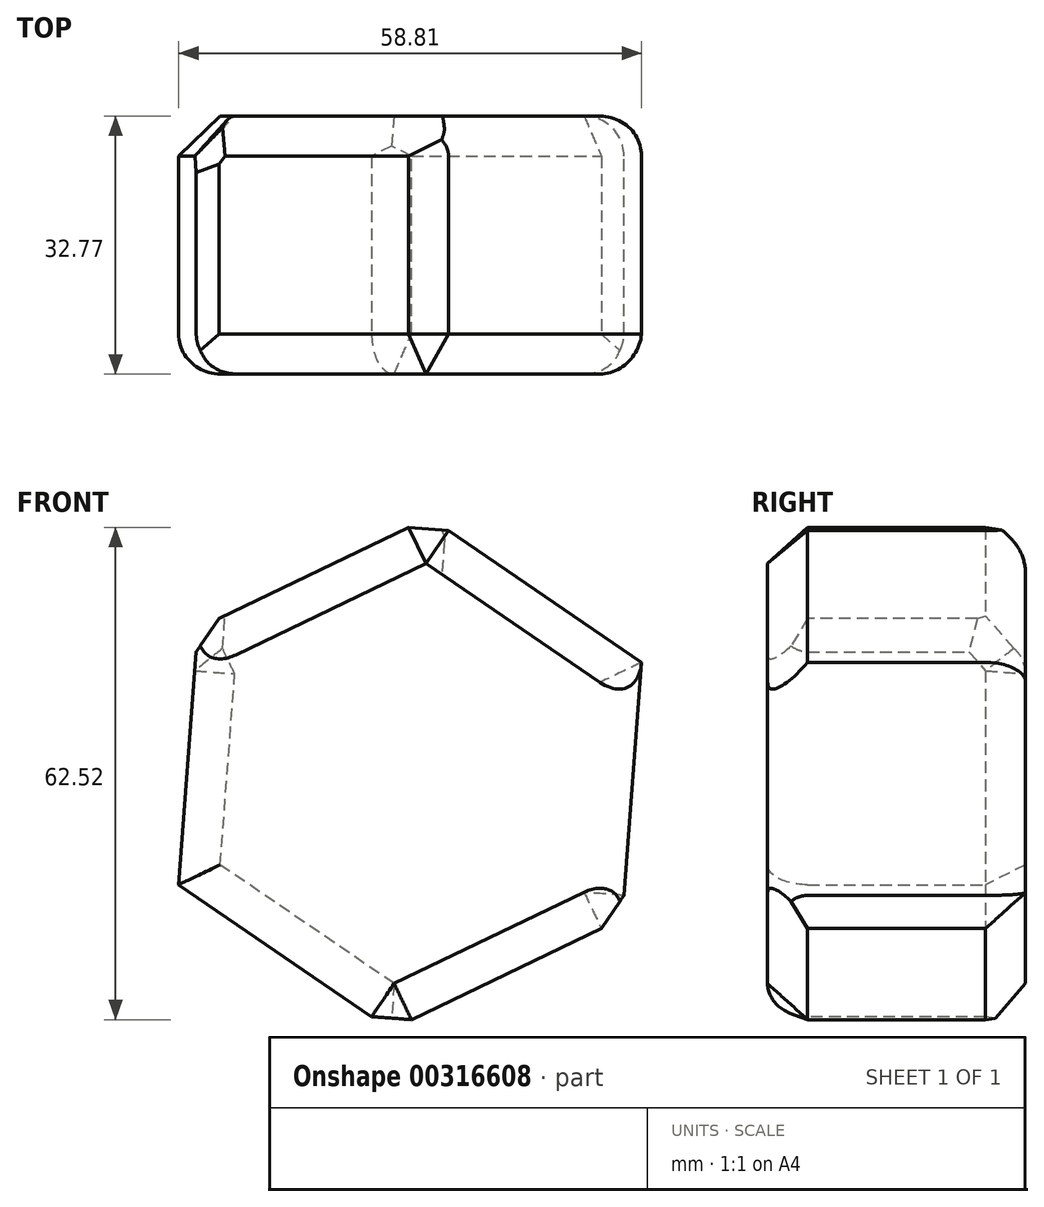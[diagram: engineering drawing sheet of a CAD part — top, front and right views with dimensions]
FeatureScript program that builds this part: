
annotation { "Feature Type Name" : "Feature", "Feature Type Description" : "" }
export const myFeature = defineFeature(function(context is Context, id is Id, definition is map)
    precondition{}
    {
        {
            var Q0;
            Q0=qCreatedBy(makeId("Front.planeOp"),FACE);
            var sketch = newSketch(context, id + "F0", { "sketchPlane" : qUnion([Q0])});
            skCircle(sketch, "E0", {"center": v(12.1, 17.74) * mm, "radius": 53.66 * mm});
            skCircle(sketch, "E1.cCircle", {"center": v(12.1, 17.74) * mm, "radius": 28.25 * mm, "construction": true});
            skLineSegment(sketch, "E1.0", {"start": v(9.62, -14.79) * mm, "end": v(-17.31, 3.61) * mm});
            skLineSegment(sketch, "E1.1", {"start": v(-17.31, 3.61) * mm, "end": v(-14.85, 36.15) * mm});
            skLineSegment(sketch, "E1.2", {"start": v(-14.85, 36.15) * mm, "end": v(14.56, 50.27) * mm});
            skLineSegment(sketch, "E1.3", {"start": v(14.56, 50.27) * mm, "end": v(41.5, 31.87) * mm});
            skLineSegment(sketch, "E1.4", {"start": v(41.5, 31.87) * mm, "end": v(39.03, -0.66) * mm});
            skLineSegment(sketch, "E1.5", {"start": v(39.03, -0.66) * mm, "end": v(9.62, -14.79) * mm});
            skPoint(sketch, "E1.0.midPoint", {"position": v(-3.84, -5.59) * mm});
            skSolve(sketch);
        }
        {
            var Q0;
            Q0=makeQuery(id+"F0.imprint","IMPRINT",FACE,{"disambiguationData":[TD([[makeQuery(id+"F0.imprint","IMPRINT",EDGE,{"derivedFrom":sQuery(id+"F0.wireOp",EDGE,"E1.0")}),-1.0]])]});
            extrude(context, id + "F1", {"entities" : qUnion([Q0]), "depth" : 32.77 * mm});
        }
        {
            var Q0;
            Q0=makeQuery(id+"F1.opExtrude","CAP_EDGE",EDGE,{"disambiguationData":[OSD([sQuery(id+"F0.wireOp",EDGE,"E1.3")])],"isStart":false});
            var Q1;
            Q1=makeQuery(id+"F1.opExtrude","SWEPT_FACE",FACE,{"disambiguationData":[OSD([sQuery(id+"F0.wireOp",EDGE,"E1.2")])]});
            chamfer(context, id + "F2", {"entities" : qUnion([Q0, Q1]), "width" : 5.08 * mm, "tangentPropagation" : true});
        }
        {
            var Q0;
            Q0=makeQuery(id+"F1.opExtrude","CAP_EDGE",EDGE,{"disambiguationData":[OSD([sQuery(id+"F0.wireOp",EDGE,"E1.1")])],"isStart":false});
            var Q1;
            Q1=makeQuery(id+"F1.opExtrude","CAP_EDGE",EDGE,{"disambiguationData":[OSD([sQuery(id+"F0.wireOp",EDGE,"E1.0")])],"isStart":false});
            fillet(context, id + "F3", {"entities" : qUnion([Q0, Q1]), "radius" : 5.08 * mm, "tangentPropagation" : true, "allowEdgeOverflow" : false});
        }
        {
            var Q0;
            Q0=makeQuery(id+"F1.opExtrude","CAP_EDGE",EDGE,{"disambiguationData":[OSD([sQuery(id+"F0.wireOp",EDGE,"E1.5")])],"isStart":false});
            chamfer(context, id + "F4", {"entities" : qUnion([Q0]), "width" : 5.08 * mm, "tangentPropagation" : true});
        }
        {
            var Q0;
            Q0=makeQuery(id+"F1.opExtrude","CAP_EDGE",EDGE,{"disambiguationData":[OSD([sQuery(id+"F0.wireOp",EDGE,"E1.4")])],"isStart":false});
            var Q1;
            Q1=makeQuery(id+"F1.opExtrude","CAP_EDGE",EDGE,{"disambiguationData":[OSD([sQuery(id+"F0.wireOp",EDGE,"E1.4")])],"isStart":true});
            var Q2;
            Q2=makeQuery(id+"F1.opExtrude","CAP_EDGE",EDGE,{"disambiguationData":[OSD([sQuery(id+"F0.wireOp",EDGE,"E1.3")])],"isStart":true});
            var Q3;
            {var subQ0=sQuery(id+"F0.wireOp",EDGE,"E1.2");Q3=makeQuery(id+"F2.opChamfer","BLEND_EDGE",EDGE,{"blendedFrom":[makeQuery(id+"F1.opExtrude","CAP_EDGE",EDGE,{"disambiguationData":[OSD([subQ0])],"isStart":true}),makeQuery(id+"F1.opExtrude","CAP_FACE",FACE,{"disambiguationData":[OSD([sQuery(id+"F0.wireOp",EDGE,"E1.0"),sQuery(id+"F0.wireOp",EDGE,"E1.1"),subQ0,sQuery(id+"F0.wireOp",EDGE,"E1.3"),sQuery(id+"F0.wireOp",EDGE,"E1.4"),sQuery(id+"F0.wireOp",EDGE,"E1.5")])],"isStart":true})],"blendedInto":[makeQuery(id+"F1.opExtrude","CAP_FACE",FACE,{"disambiguationData":[OSD([sQuery(id+"F0.wireOp",EDGE,"E1.0"),sQuery(id+"F0.wireOp",EDGE,"E1.1"),subQ0,sQuery(id+"F0.wireOp",EDGE,"E1.3"),sQuery(id+"F0.wireOp",EDGE,"E1.4"),sQuery(id+"F0.wireOp",EDGE,"E1.5")])],"isStart":true})]});}
            fillet(context, id + "F5", {"entities" : qUnion([Q0, Q1, Q2, Q3]), "radius" : 5.08 * mm, "tangentPropagation" : true, "allowEdgeOverflow" : false});
        }
        {
            var Q0;
            Q0=makeQuery(id+"F1.opExtrude","CAP_EDGE",EDGE,{"disambiguationData":[OSD([sQuery(id+"F0.wireOp",EDGE,"E1.1")])],"isStart":true});
            var Q1;
            Q1=makeQuery(id+"F1.opExtrude","CAP_EDGE",EDGE,{"disambiguationData":[OSD([sQuery(id+"F0.wireOp",EDGE,"E1.0")])],"isStart":true});
            var Q2;
            Q2=makeQuery(id+"F1.opExtrude","CAP_EDGE",EDGE,{"disambiguationData":[OSD([sQuery(id+"F0.wireOp",EDGE,"E1.5")])],"isStart":true});
            chamfer(context, id + "F6", {"entities" : qUnion([Q0, Q1, Q2]), "width" : 5.08 * mm, "tangentPropagation" : true});
        }
    });
